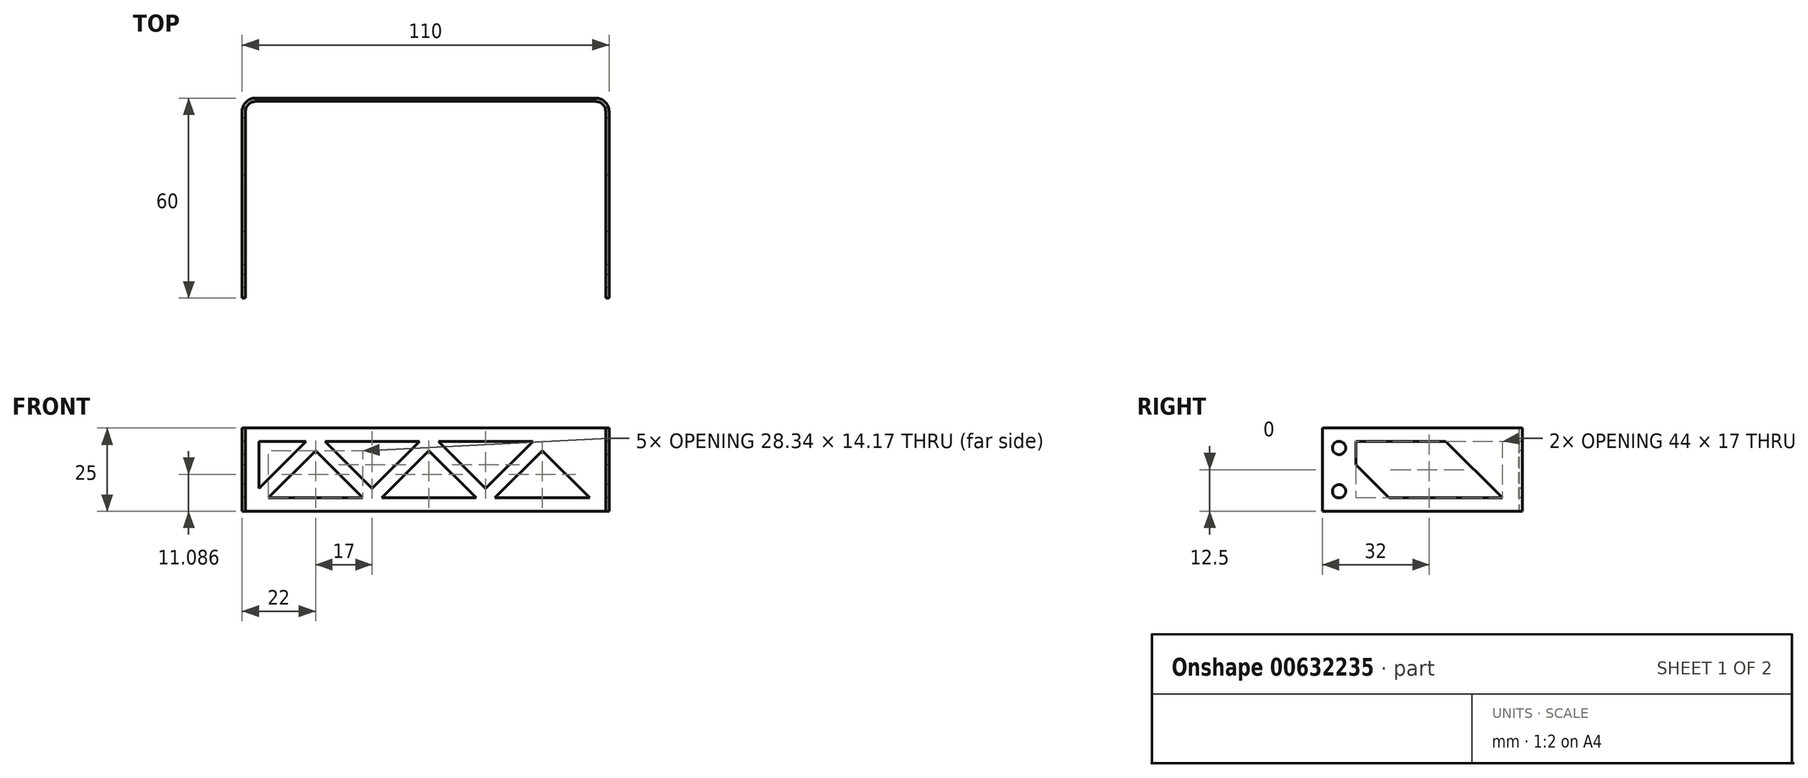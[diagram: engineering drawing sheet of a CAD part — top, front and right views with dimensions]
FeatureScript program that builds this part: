
annotation { "Feature Type Name" : "Feature", "Feature Type Description" : "" }
export const myFeature = defineFeature(function(context is Context, id is Id, definition is map)
    precondition{}
    {
        {
            var Q0;
            Q0=qCreatedBy(makeId("Top.planeOp"),FACE);
            var sketch = newSketch(context, id + "F0", { "sketchPlane" : qUnion([Q0])});
            skLineSegment(sketch, "E0", {"start": v(0, 0) * mm, "end": v(0, 56) * mm});
            skLineSegment(sketch, "E1", {"start": v(-3, 59) * mm, "end": v(-105, 59) * mm});
            skLineSegment(sketch, "E2", {"start": v(-108, 56) * mm, "end": v(-108, 0) * mm});
            skLineSegment(sketch, "E3.0", {"start": v(-109, 56) * mm, "end": v(-109, 0) * mm});
            skLineSegment(sketch, "E3.1", {"start": v(-3, 60) * mm, "end": v(-105, 60) * mm});
            skLineSegment(sketch, "E3.2", {"start": v(1, 0) * mm, "end": v(1, 56) * mm});
            skLineSegment(sketch, "E4.bottom", {"start": v(-109, 0) * mm, "end": v(-108, 0) * mm});
            skLineSegment(sketch, "E5", {"start": v(1, 0) * mm, "end": v(0, 0) * mm});
            skPoint(sketch, "E6.visualSharp", {"position": v(-108, 59) * mm});
            skArc(sketch, "E6.filletArc", {"start": v(-105, 59) * mm, "mid": v(-107.12, 58.12) * mm, "end": v(-108, 56) * mm});
            skPoint(sketch, "E7.visualSharp", {"position": v(0, 59) * mm});
            skArc(sketch, "E7.filletArc", {"start": v(0, 56) * mm, "mid": v(-0.88, 58.12) * mm, "end": v(-3, 59) * mm});
            skPoint(sketch, "E8.visualSharp", {"position": v(-109, 60) * mm});
            skArc(sketch, "E8.filletArc", {"start": v(-105, 60) * mm, "mid": v(-107.83, 58.83) * mm, "end": v(-109, 56) * mm});
            skPoint(sketch, "E9.visualSharp", {"position": v(1, 60) * mm});
            skArc(sketch, "E9.filletArc", {"start": v(1, 56) * mm, "mid": v(-0.17, 58.83) * mm, "end": v(-3, 60) * mm});
            skSolve(sketch);
        }
        {
            var Q0;
            Q0=makeQuery(id+"F0.imprint","IMPRINT",FACE,{"disambiguationData":[TD([[makeQuery(id+"F0.imprint","IMPRINT",EDGE,{"derivedFrom":sQuery(id+"F0.wireOp",EDGE,"E0")}),-1.0]])]});
            extrude(context, id + "F1", {"entities" : qUnion([Q0]), "depth" : 25 * mm, "offsetDistance" : 25 * mm});
        }
        {
            var Q0;
            Q0=makeQuery(id+"F1.opExtrude","SWEPT_FACE",FACE,{"disambiguationData":[OSD([sQuery(id+"F0.wireOp",EDGE,"E1")])]});
            var sketch = newSketch(context, id + "F2", { "sketchPlane" : qUnion([Q0])});
            skLineSegment(sketch, "E10", {"start": v(-104, 4) * mm, "end": v(-87, 21) * mm, "construction": true});
            skLineSegment(sketch, "E11", {"start": v(-87, 21) * mm, "end": v(-70, 4) * mm, "construction": true});
            skLineSegment(sketch, "E12", {"start": v(-70, 4) * mm, "end": v(-53, 21) * mm, "construction": true});
            skLineSegment(sketch, "E13", {"start": v(-53, 21) * mm, "end": v(-36, 4) * mm, "construction": true});
            skLineSegment(sketch, "E14", {"start": v(-70, 4) * mm, "end": v(-116.6, 4) * mm, "construction": true});
            skLineSegment(sketch, "E15", {"start": v(-87, 21) * mm, "end": v(-150.6, 21) * mm, "construction": true});
            skLineSegment(sketch, "E16", {"start": v(-70, 4) * mm, "end": v(16.38, 4) * mm, "construction": true});
            skLineSegment(sketch, "E17", {"start": v(-36, 4) * mm, "end": v(-19, 21) * mm, "construction": true});
            skLineSegment(sketch, "E18", {"start": v(-19, 21) * mm, "end": v(-3, 5) * mm, "construction": true});
            skLineSegment(sketch, "E19.0", {"start": v(-19, 18.17) * mm, "end": v(-10.41, 9.59) * mm});
            skLineSegment(sketch, "E19.1", {"start": v(-36, 1.17) * mm, "end": v(-19, 18.17) * mm});
            skLineSegment(sketch, "E19.2", {"start": v(-102.59, 2.59) * mm, "end": v(-87, 18.17) * mm});
            skLineSegment(sketch, "E19.3", {"start": v(-87, 18.17) * mm, "end": v(-70, 1.17) * mm});
            skLineSegment(sketch, "E19.4", {"start": v(-70, 1.17) * mm, "end": v(-53, 18.17) * mm});
            skLineSegment(sketch, "E19.5", {"start": v(-53, 18.17) * mm, "end": v(-36, 1.17) * mm});
            skLineSegment(sketch, "E20.0", {"start": v(-19, 23.83) * mm, "end": v(-7.59, 12.41) * mm});
            skLineSegment(sketch, "E20.1", {"start": v(-36, 6.83) * mm, "end": v(-19, 23.83) * mm});
            skLineSegment(sketch, "E20.2", {"start": v(-105.41, 5.41) * mm, "end": v(-87, 23.83) * mm});
            skLineSegment(sketch, "E20.3", {"start": v(-87, 23.83) * mm, "end": v(-70, 6.83) * mm});
            skLineSegment(sketch, "E20.4", {"start": v(-70, 6.83) * mm, "end": v(-53, 23.83) * mm});
            skLineSegment(sketch, "E20.5", {"start": v(-53, 23.83) * mm, "end": v(-36, 6.83) * mm});
            skLineSegment(sketch, "E21", {"start": v(-104, 4) * mm, "end": v(-70, 4) * mm});
            skLineSegment(sketch, "E22", {"start": v(-36, 4) * mm, "end": v(-3, 4) * mm});
            skLineSegment(sketch, "E23", {"start": v(-3, 4) * mm, "end": v(-3, 5) * mm});
            skLineSegment(sketch, "E24", {"start": v(-87, 21) * mm, "end": v(-53, 21) * mm});
            skLineSegment(sketch, "E25", {"start": v(-19, 21) * mm, "end": v(-53, 21) * mm});
            skLineSegment(sketch, "E26", {"start": v(-19, 21) * mm, "end": v(-3, 21) * mm});
            skLineSegment(sketch, "E27", {"start": v(-3, 21) * mm, "end": v(-3, 5) * mm});
            skLineSegment(sketch, "E28", {"start": v(-104, 4) * mm, "end": v(-104, 21) * mm});
            skLineSegment(sketch, "E29", {"start": v(-104, 21) * mm, "end": v(-87, 21) * mm});
            skLineSegment(sketch, "E30", {"start": v(-70, 4) * mm, "end": v(-36, 4) * mm});
            skLineSegment(sketch, "E31", {"start": v(-10.41, 9.59) * mm, "end": v(-3, 2.17) * mm});
            skSolve(sketch);
        }
        {
            var Q0;
            {var subQ0=sQuery(id+"F2.wireOp",EDGE,"E20.4");var subQ1=sQuery(id+"F2.wireOp",EDGE,"E20.3");var subQ2=makeQuery(id+"F2.imprint","INTERSECT",VERTEX,{"derivedFrom":[subQ1,subQ0]});Q0=makeQuery(id+"F2.imprint","IMPRINT",FACE,{"disambiguationData":[TD([[makeQuery(id+"F2.imprint","IMPRINT",EDGE,{"disambiguationData":[TD([[subQ2,1.0]])],"derivedFrom":subQ1}),1.0]])]});}
            var Q1;
            {var subQ0=sQuery(id+"F2.wireOp",EDGE,"E20.5");var subQ1=sQuery(id+"F2.wireOp",EDGE,"E20.1");var subQ2=makeQuery(id+"F2.imprint","INTERSECT",VERTEX,{"derivedFrom":[subQ1,subQ0]});Q1=makeQuery(id+"F2.imprint","IMPRINT",FACE,{"disambiguationData":[TD([[makeQuery(id+"F2.imprint","IMPRINT",EDGE,{"disambiguationData":[TD([[subQ2,-1.0]])],"derivedFrom":subQ1}),1.0]])]});}
            var Q2;
            {var subQ0=sQuery(id+"F2.wireOp",EDGE,"E19.3");var subQ1=sQuery(id+"F2.wireOp",EDGE,"E19.2");var subQ2=makeQuery(id+"F2.imprint","INTERSECT",VERTEX,{"derivedFrom":[subQ1,subQ0]});Q2=makeQuery(id+"F2.imprint","IMPRINT",FACE,{"disambiguationData":[TD([[makeQuery(id+"F2.imprint","IMPRINT",EDGE,{"disambiguationData":[TD([[subQ2,1.0]])],"derivedFrom":subQ1}),-1.0]])]});}
            var Q3;
            {var subQ0=sQuery(id+"F2.wireOp",EDGE,"E28");var subQ1=sQuery(id+"F2.wireOp",EDGE,"E20.2");var subQ2=makeQuery(id+"F2.imprint","INTERSECT",VERTEX,{"derivedFrom":[subQ1,subQ0]});Q3=makeQuery(id+"F2.imprint","IMPRINT",FACE,{"disambiguationData":[TD([[makeQuery(id+"F2.imprint","IMPRINT",EDGE,{"disambiguationData":[TD([[subQ2,-1.0]])],"derivedFrom":subQ1}),1.0]])]});}
            var Q4;
            {var subQ0=sQuery(id+"F2.wireOp",EDGE,"E19.5");var subQ1=sQuery(id+"F2.wireOp",EDGE,"E19.4");var subQ2=makeQuery(id+"F2.imprint","INTERSECT",VERTEX,{"derivedFrom":[subQ1,subQ0]});Q4=makeQuery(id+"F2.imprint","IMPRINT",FACE,{"disambiguationData":[TD([[makeQuery(id+"F2.imprint","IMPRINT",EDGE,{"disambiguationData":[TD([[subQ2,1.0]])],"derivedFrom":subQ1}),-1.0]])]});}
            var Q5;
            {var subQ6=sQuery(id+"F2.wireOp",EDGE,"E19.0");Q5=makeQuery(id+"F2.imprint","IMPRINT",FACE,{"disambiguationData":[TD([[makeQuery(id+"F2.imprint","IMPRINT",EDGE,{"derivedFrom":subQ6}),-1.0]])]});}
            extrude(context, id + "F3", {"entities" : qUnion([Q0, Q1, Q2, Q3, Q4, Q5]), "operationType" : NewBodyOperationType.REMOVE, "oppositeDirection" : true, "depth" : 25 * mm, "offsetDistance" : 25 * mm});
        }
        {
            var Q0;
            Q0=makeQuery(id+"F1.opExtrude","SWEPT_FACE",FACE,{"disambiguationData":[OSD([sQuery(id+"F0.wireOp",EDGE,"E3.0")])]});
            var sketch = newSketch(context, id + "F4", { "sketchPlane" : qUnion([Q0])});
            skCircle(sketch, "E32", {"center": v(-5, 19) * mm, "radius": 2 * mm});
            skCircle(sketch, "E33", {"center": v(-5, 6) * mm, "radius": 2 * mm});
            skLineSegment(sketch, "E34", {"start": v(-5, 19) * mm, "end": v(-5, 6) * mm, "construction": true});
            skLineSegment(sketch, "E35", {"start": v(0, 21) * mm, "end": v(-60.34, 21) * mm});
            skLineSegment(sketch, "E36", {"start": v(0, 4) * mm, "end": v(-60.1, 4) * mm});
            skLineSegment(sketch, "E37", {"start": v(-54, 4) * mm, "end": v(-37, 21) * mm});
            skLineSegment(sketch, "E38", {"start": v(-37, 21) * mm, "end": v(-20, 4) * mm});
            skLineSegment(sketch, "E39", {"start": v(-10, 4) * mm, "end": v(-10, 21) * mm});
            skLineSegment(sketch, "E40", {"start": v(-20, 4) * mm, "end": v(-10, 14) * mm});
            skSolve(sketch);
        }
        {
            var Q0;
            Q0=makeQuery(id+"F4.imprint","IMPRINT",FACE,{"disambiguationData":[TD([[makeQuery(id+"F4.imprint","IMPRINT",EDGE,{"derivedFrom":sQuery(id+"F4.wireOp",EDGE,"E32")}),1.0]])]});
            var Q1;
            Q1=makeQuery(id+"F4.imprint","IMPRINT",FACE,{"disambiguationData":[TD([[makeQuery(id+"F4.imprint","IMPRINT",EDGE,{"derivedFrom":sQuery(id+"F4.wireOp",EDGE,"E33")}),1.0]])]});
            var Q2;
            {var subQ0=sQuery(id+"F4.wireOp",EDGE,"E38");Q2=makeQuery(id+"F4.imprint","IMPRINT",FACE,{"disambiguationData":[TD([[makeQuery(id+"F4.imprint","IMPRINT",EDGE,{"derivedFrom":subQ0}),1.0]])]});}
            var Q3;
            {var subQ0=sQuery(id+"F4.wireOp",EDGE,"E37");Q3=makeQuery(id+"F4.imprint","IMPRINT",FACE,{"disambiguationData":[TD([[makeQuery(id+"F4.imprint","IMPRINT",EDGE,{"derivedFrom":subQ0}),-1.0]])]});}
            extrude(context, id + "F5", {"entities" : qUnion([Q0, Q1, Q2, Q3]), "operationType" : NewBodyOperationType.REMOVE, "oppositeDirection" : true, "depth" : 200 * mm, "offsetDistance" : 25 * mm});
        }
    });
